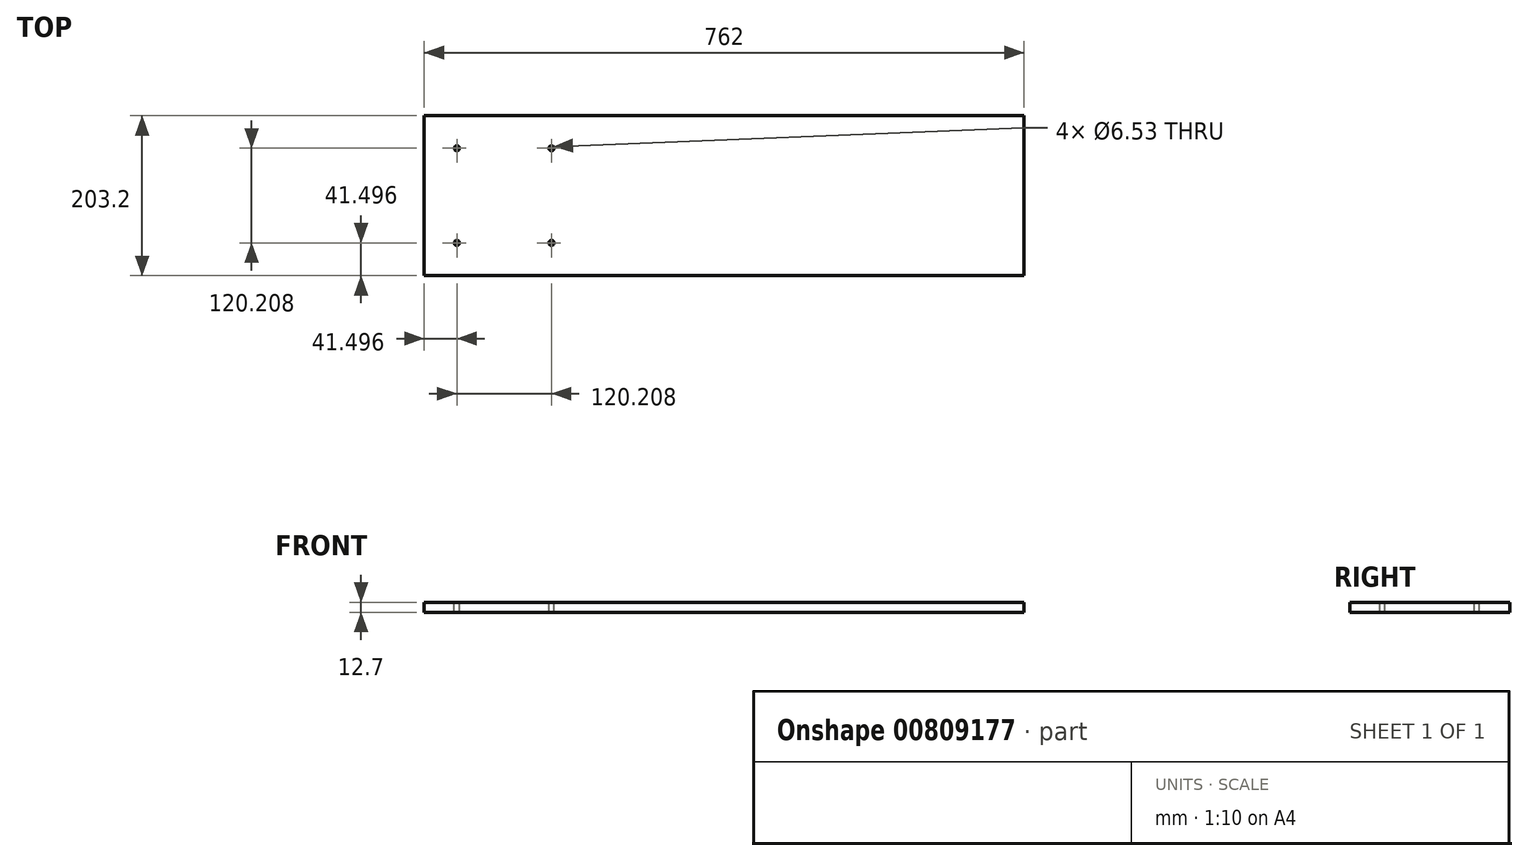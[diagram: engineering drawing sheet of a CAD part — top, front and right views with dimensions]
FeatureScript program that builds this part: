
annotation { "Feature Type Name" : "Feature", "Feature Type Description" : "" }
export const myFeature = defineFeature(function(context is Context, id is Id, definition is map)
    precondition{}
    {
        {
            var Q0;
            Q0=qCreatedBy(makeId("Top.planeOp"),FACE);
            var sketch = newSketch(context, id + "F0", { "sketchPlane" : qUnion([Q0])});
            skLineSegment(sketch, "E0.bottom", {"start": v(-381, 101.6) * mm, "end": v(381, 101.6) * mm});
            skLineSegment(sketch, "E0.top", {"start": v(-381, -101.6) * mm, "end": v(381, -101.6) * mm});
            skLineSegment(sketch, "E0.left", {"start": v(-381, 101.6) * mm, "end": v(-381, -101.6) * mm});
            skLineSegment(sketch, "E0.right", {"start": v(381, 101.6) * mm, "end": v(381, -101.6) * mm});
            skSolve(sketch);
        }
        {
            var Q0;
            {var subQ0=sQuery(id+"F0.wireOp",EDGE,"E0.left");Q0=makeQuery(id+"F0.imprint","IMPRINT",FACE,{"disambiguationData":[TD([[makeQuery(id+"F0.imprint","IMPRINT",EDGE,{"derivedFrom":subQ0}),1.0]])]});}
            var Q1;
            {var subQ0=sQuery(id+"F0.wireOp",EDGE,"E0.right");Q1=makeQuery(id+"F0.imprint","IMPRINT",FACE,{"disambiguationData":[TD([[makeQuery(id+"F0.imprint","IMPRINT",EDGE,{"derivedFrom":subQ0}),-1.0]])]});}
            extrude(context, id + "F1", {"entities" : qUnion([Q0, Q1]), "depth" : 12.7 * mm, "offsetDistance" : 25.4 * mm});
        }
        {
            var Q0;
            Q0=makeQuery(id+"F1.opExtrude","CAP_FACE",FACE,{"disambiguationData":[OSD([sQuery(id+"F0.wireOp",EDGE,"E0.bottom"),sQuery(id+"F0.wireOp",EDGE,"E0.top"),sQuery(id+"F0.wireOp",EDGE,"E0.left"),sQuery(id+"F0.wireOp",EDGE,"E0.right")])],"isStart":false});
            var sketch = newSketch(context, id + "F2", { "sketchPlane" : qUnion([Q0])});
            skPoint(sketch, "E1", {"position": v(-279.4, 0) * mm});
            skPoint(sketch, "E2", {"position": v(-339.5, -60.1) * mm});
            skCircle(sketch, "E3", {"center": v(-279.4, 0) * mm, "radius": 85 * mm});
            skLineSegment(sketch, "E4", {"start": v(-279.4, 0) * mm, "end": v(-279.4, -85) * mm});
            skLineSegment(sketch, "E5", {"start": v(-279.4, 0) * mm, "end": v(-339.5, -60.1) * mm});
            skPoint(sketch, "E6.1.0", {"position": v(-219.3, -60.1) * mm});
            skPoint(sketch, "E6.2.0", {"position": v(-219.3, 60.1) * mm});
            skPoint(sketch, "E6.3.0", {"position": v(-339.5, 60.1) * mm});
            skSolve(sketch);
        }
        {
            var Q0;
            Q0=sQuery(id+"F2.wireOp",VERTEX,"E2");
            var Q1;
            Q1=sQuery(id+"F2.wireOp",VERTEX,"E6.3.0");
            var Q2;
            Q2=sQuery(id+"F2.wireOp",VERTEX,"E6.2.0");
            var Q3;
            Q3=sQuery(id+"F2.wireOp",VERTEX,"E6.1.0");
            var Q4;
            Q4=makeQuery(id+"F1.opExtrude","SWEPT_BODY",BODY,{"disambiguationData":[OSD([sQuery(id+"F0.wireOp",EDGE,"E0.bottom"),sQuery(id+"F0.wireOp",EDGE,"E0.top"),sQuery(id+"F0.wireOp",EDGE,"E0.left"),sQuery(id+"F0.wireOp",EDGE,"E0.right")])]});
            hole(context, id + "F3", {"style" : HoleStyle.SIMPLE, "endStyle" : HoleEndStyle.THROUGH, "standardTappedOrClearance" : lookupTablePath({ "standard" : "ANSI", "engagement" : "75%", "pitch" : "18 tpi", "size" : "5/16", "type" : "Tapped" }), "standardBlindInLast" : lookupTablePath({ "standard" : "ANSI", "engagement" : "75%", "pitch" : "18 tpi", "size" : "5/16", "type" : "Tapped" }), "holeDiameter" : 6.53 * mm, "majorDiameter" : 7.94 * mm, "showTappedDepth" : true, "isTappedThrough" : true, "tappedDepth" : 12.7 * mm, "tapClearance" : 3, "locations" : qUnion([Q0, Q1, Q2, Q3]), "scope" : qUnion([Q4])});
        }
    });
